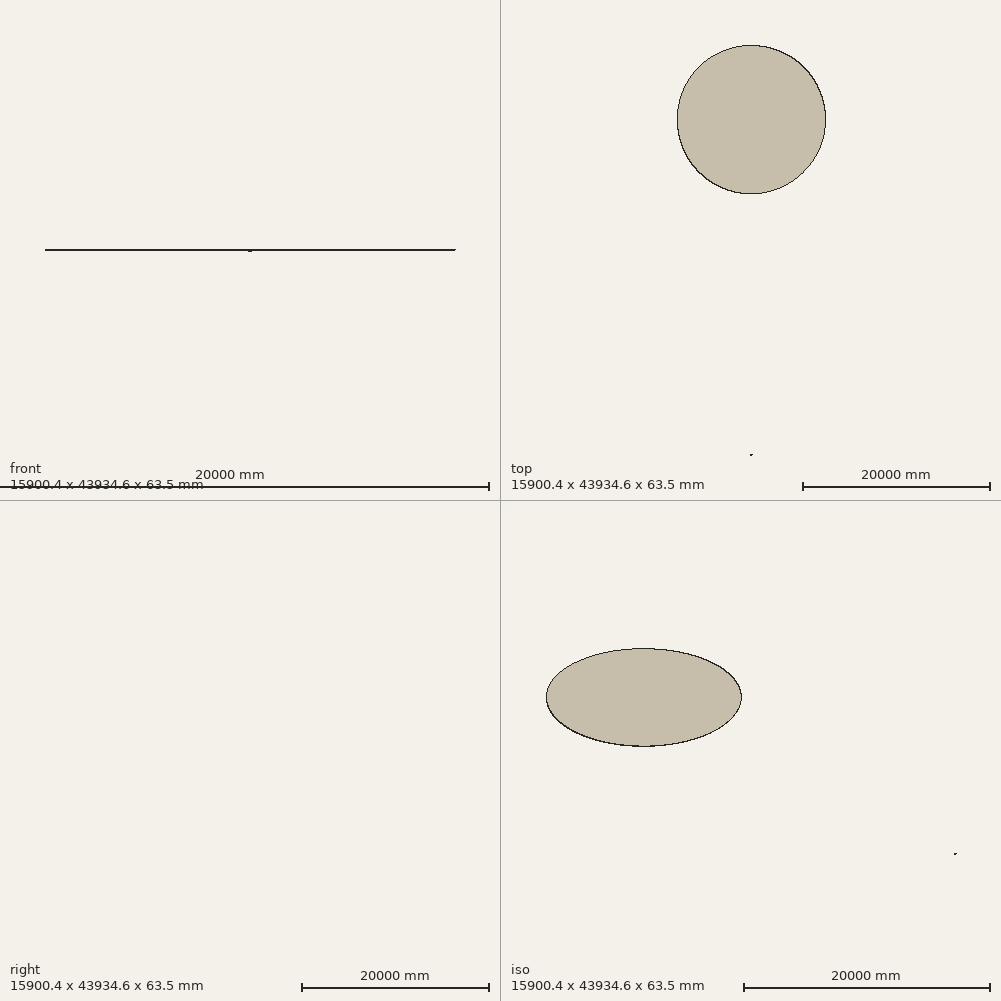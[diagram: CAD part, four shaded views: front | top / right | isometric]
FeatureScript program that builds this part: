
annotation { "Feature Type Name" : "Feature", "Feature Type Description" : "" }
export const myFeature = defineFeature(function(context is Context, id is Id, definition is map)
    precondition{}
    {
        {
            var Q0;
            Q0=qCreatedBy(makeId("Top.planeOp"),FACE);
            var sketch = newSketch(context, id + "F0", { "sketchPlane" : qUnion([Q0])});
            skLineSegment(sketch, "E0.bottom", {"start": v(76.45, 50.37) * mm, "end": v(-76.45, 50.37) * mm});
            skLineSegment(sketch, "E0.top", {"start": v(76.45, -50.37) * mm, "end": v(-76.45, -50.37) * mm});
            skLineSegment(sketch, "E0.left", {"start": v(76.45, 50.37) * mm, "end": v(76.45, -50.37) * mm});
            skLineSegment(sketch, "E0.right", {"start": v(-76.45, 50.37) * mm, "end": v(-76.45, -50.37) * mm});
            skPoint(sketch, "E0.middle", {"position": v(0, 0) * mm});
            skLineSegment(sketch, "E1.bottom", {"start": v(60.84, 31.34) * mm, "end": v(-60.84, 31.34) * mm});
            skLineSegment(sketch, "E1.top", {"start": v(60.84, -31.34) * mm, "end": v(-60.84, -31.34) * mm});
            skLineSegment(sketch, "E1.left", {"start": v(60.84, 31.34) * mm, "end": v(60.84, -31.34) * mm});
            skLineSegment(sketch, "E1.right", {"start": v(-60.84, 31.34) * mm, "end": v(-60.84, -31.34) * mm});
            skSolve(sketch);
        }
        {
            var Q0;
            Q0=makeQuery(id+"F0.imprint","IMPRINT",FACE,{"disambiguationData":[TD([[makeQuery(id+"F0.imprint","IMPRINT",EDGE,{"derivedFrom":sQuery(id+"F0.wireOp",EDGE,"E0.bottom")}),1.0]])]});
            extrude(context, id + "F1", {"entities" : qUnion([Q0]), "depth" : 38.1 * mm});
        }
        {
            var Q0;
            Q0=makeQuery(id+"F0.imprint","IMPRINT",FACE,{"disambiguationData":[TD([[makeQuery(id+"F0.imprint","IMPRINT",EDGE,{"derivedFrom":sQuery(id+"F0.wireOp",EDGE,"E1.bottom")}),1.0]])]});
            extrude(context, id + "F2", {"entities" : qUnion([Q0]), "operationType" : NewBodyOperationType.ADD, "depth" : 0.25 * mm});
        }
        {
            var Q0;
            Q0=makeQuery(id+"F1.opExtrude","SWEPT_EDGE",EDGE,{"disambiguationData":[OSD([sQuery(id+"F0.wireOp",EDGE,"E1.bottom"),sQuery(id+"F0.wireOp",EDGE,"E1.right")])]});
            var Q1;
            Q1=makeQuery(id+"F1.opExtrude","SWEPT_EDGE",EDGE,{"disambiguationData":[OSD([sQuery(id+"F0.wireOp",EDGE,"E0.bottom"),sQuery(id+"F0.wireOp",EDGE,"E0.right")])]});
            var Q2;
            Q2=makeQuery(id+"F1.opExtrude","SWEPT_EDGE",EDGE,{"disambiguationData":[OSD([sQuery(id+"F0.wireOp",EDGE,"E0.top"),sQuery(id+"F0.wireOp",EDGE,"E0.right")])]});
            var Q3;
            Q3=makeQuery(id+"F1.opExtrude","SWEPT_EDGE",EDGE,{"disambiguationData":[OSD([sQuery(id+"F0.wireOp",EDGE,"E0.top"),sQuery(id+"F0.wireOp",EDGE,"E0.left")])]});
            var Q4;
            Q4=makeQuery(id+"F1.opExtrude","SWEPT_EDGE",EDGE,{"disambiguationData":[OSD([sQuery(id+"F0.wireOp",EDGE,"E1.bottom"),sQuery(id+"F0.wireOp",EDGE,"E1.left")])]});
            var Q5;
            Q5=makeQuery(id+"F1.opExtrude","SWEPT_EDGE",EDGE,{"disambiguationData":[OSD([sQuery(id+"F0.wireOp",EDGE,"E1.top"),sQuery(id+"F0.wireOp",EDGE,"E1.right")])]});
            var Q6;
            Q6=makeQuery(id+"F1.opExtrude","SWEPT_EDGE",EDGE,{"disambiguationData":[OSD([sQuery(id+"F0.wireOp",EDGE,"E1.top"),sQuery(id+"F0.wireOp",EDGE,"E1.left")])]});
            var Q7;
            Q7=makeQuery(id+"F1.opExtrude","SWEPT_EDGE",EDGE,{"disambiguationData":[OSD([sQuery(id+"F0.wireOp",EDGE,"E0.bottom"),sQuery(id+"F0.wireOp",EDGE,"E0.left")])]});
            fillet(context, id + "F3", {"entities" : qUnion([Q0, Q1, Q2, Q3, Q4, Q5, Q6, Q7]), "radius" : 12.7 * mm, "tangentPropagation" : true, "allowEdgeOverflow" : false});
        }
        {
            var Q0;
            Q0=makeQuery(id+"F1.opExtrude","CAP_FACE",FACE,{"disambiguationData":[OSD([sQuery(id+"F0.wireOp",EDGE,"E0.bottom"),sQuery(id+"F0.wireOp",EDGE,"E0.top"),sQuery(id+"F0.wireOp",EDGE,"E0.left"),sQuery(id+"F0.wireOp",EDGE,"E0.right"),sQuery(id+"F0.wireOp",EDGE,"E1.bottom"),sQuery(id+"F0.wireOp",EDGE,"E1.top"),sQuery(id+"F0.wireOp",EDGE,"E1.left"),sQuery(id+"F0.wireOp",EDGE,"E1.right")])],"isStart":false});
            cPlane(context, id + "F4", {"entities" : qUnion([Q0]), "cplaneType" : CPlaneType.OFFSET, "offset" : 0 * mm, "width" : 152.4 * mm, "height" : 152.4 * mm});
        }
        {
            var Q0;
            Q0=qCreatedBy(id+"F4.planeOp",FACE);
            var sketch = newSketch(context, id + "F5", { "sketchPlane" : qUnion([Q0])});
            skCircle(sketch, "E2", {"center": v(0, 35934.07) * mm, "radius": 7950.2 * mm});
            skCircle(sketch, "E3", {"center": v(0, 39.76) * mm, "radius": 7.95 * mm});
            skSolve(sketch);
        }
        {
            var Q0;
            Q0 = qSketchRegion(id + "F5", true);
            extrude(context, id + "F6", {"entities" : qUnion([Q0]), "operationType" : NewBodyOperationType.ADD, "depth" : 25.4 * mm});
        }
    });
